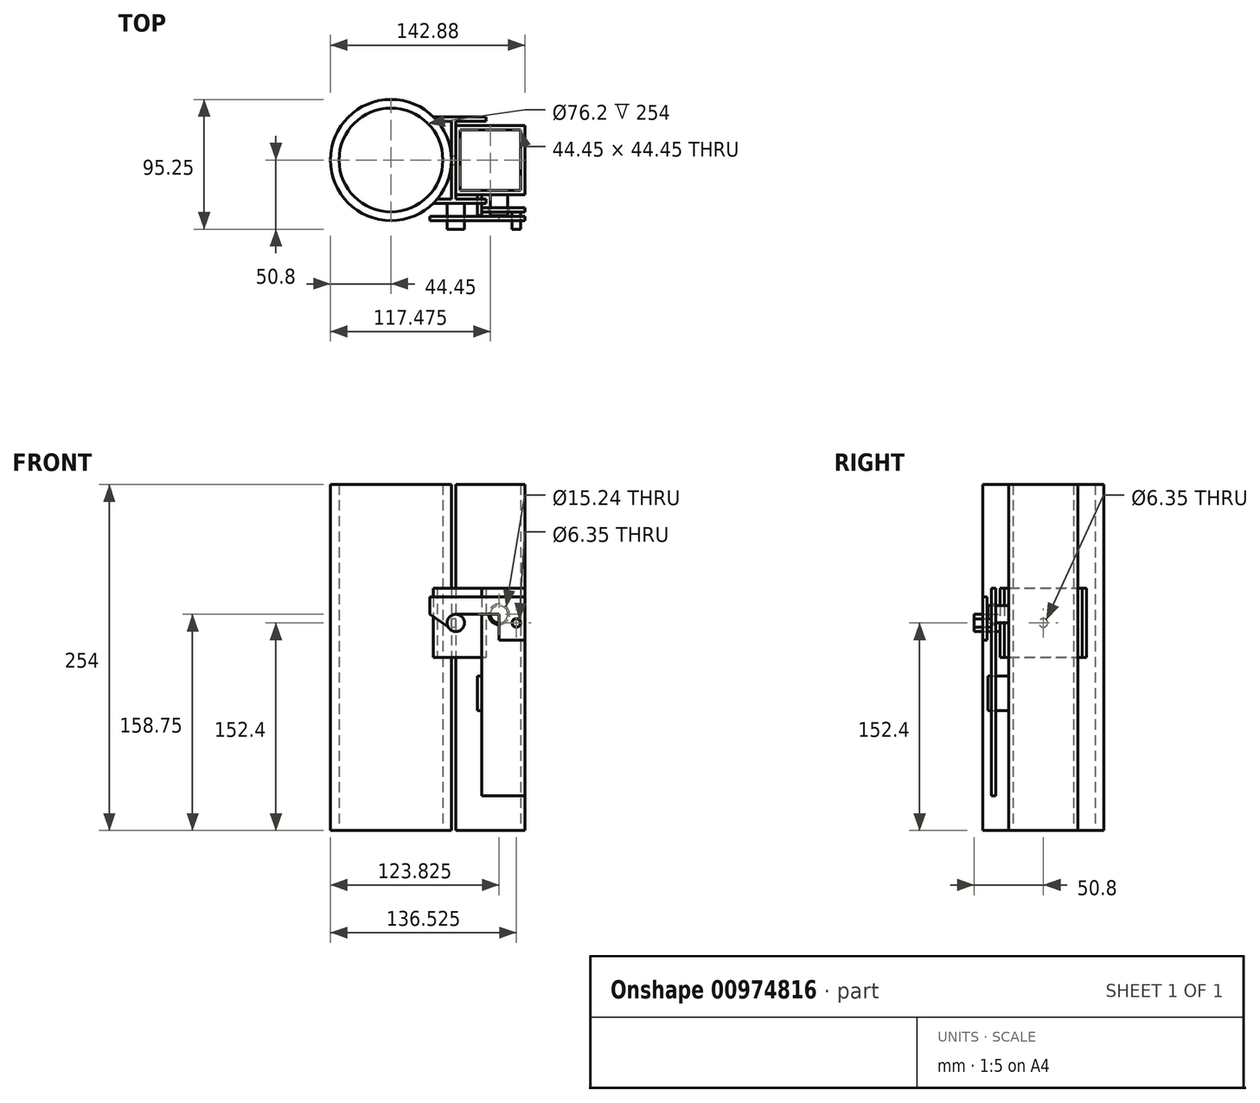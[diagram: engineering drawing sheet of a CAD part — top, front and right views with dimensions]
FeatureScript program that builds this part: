
annotation { "Feature Type Name" : "Feature", "Feature Type Description" : "" }
export const myFeature = defineFeature(function(context is Context, id is Id, definition is map)
    precondition{}
    {
        {
            var Q0;
            Q0=qCreatedBy(makeId("Top.planeOp"),FACE);
            var sketch = newSketch(context, id + "F0", { "sketchPlane" : qUnion([Q0])});
            skLineSegment(sketch, "E0", {"start": v(25.4, 31.75) * mm, "end": v(0, 31.75) * mm});
            skLineSegment(sketch, "E1", {"start": v(0, 31.75) * mm, "end": v(0, -31.75) * mm});
            skLineSegment(sketch, "E2", {"start": v(0, -31.75) * mm, "end": v(25.4, -31.75) * mm});
            skLineSegment(sketch, "E3", {"start": v(25.4, -31.75) * mm, "end": v(25.4, -28.57) * mm});
            skLineSegment(sketch, "E4", {"start": v(25.4, -28.57) * mm, "end": v(3.17, -28.57) * mm});
            skLineSegment(sketch, "E5", {"start": v(3.17, -28.57) * mm, "end": v(3.17, 28.57) * mm});
            skLineSegment(sketch, "E6", {"start": v(3.17, 28.57) * mm, "end": v(25.4, 28.57) * mm});
            skLineSegment(sketch, "E7", {"start": v(25.4, 28.57) * mm, "end": v(25.4, 31.75) * mm});
            skCircle(sketch, "E8", {"center": v(-44.45, 0) * mm, "radius": 44.45 * mm, "construction": true});
            skLineSegment(sketch, "E9", {"start": v(0, 28.57) * mm, "end": v(-10.4, 28.57) * mm});
            skLineSegment(sketch, "E10", {"start": v(0, 31.75) * mm, "end": v(-13.34, 31.75) * mm});
            skLineSegment(sketch, "E11", {"start": v(0, -28.57) * mm, "end": v(-10.4, -28.57) * mm});
            skLineSegment(sketch, "E12", {"start": v(0, -31.75) * mm, "end": v(-13.34, -31.75) * mm});
            skArc(sketch, "E13", {"start": v(-10.4, 28.57) * mm, "mid": v(-11.83, 30.2) * mm, "end": v(-13.34, 31.75) * mm});
            skArc(sketch, "E14", {"start": v(-13.34, -31.75) * mm, "mid": v(-11.83, -30.2) * mm, "end": v(-10.4, -28.57) * mm});
            skLineSegment(sketch, "E15", {"start": v(-100.23, -63.5) * mm, "end": v(128.61, -63.5) * mm, "construction": true});
            skLineSegment(sketch, "E16", {"start": v(-100.58, -69.85) * mm, "end": v(131.7, -69.85) * mm, "construction": true});
            skSolve(sketch);
        }
        {
            var Q0;
            {var subQ2=sQuery(id+"F0.wireOp",EDGE,"E9");Q0=makeQuery(id+"F0.imprint","IMPRINT",FACE,{"disambiguationData":[TD([[makeQuery(id+"F0.imprint","IMPRINT",EDGE,{"derivedFrom":subQ2}),-1.0]])]});}
            var Q1;
            {var subQ3=sQuery(id+"F0.wireOp",EDGE,"E0");Q1=makeQuery(id+"F0.imprint","IMPRINT",FACE,{"disambiguationData":[TD([[makeQuery(id+"F0.imprint","IMPRINT",EDGE,{"derivedFrom":subQ3}),1.0]])]});}
            var Q2;
            {var subQ2=sQuery(id+"F0.wireOp",EDGE,"E11");Q2=makeQuery(id+"F0.imprint","IMPRINT",FACE,{"disambiguationData":[TD([[makeQuery(id+"F0.imprint","IMPRINT",EDGE,{"derivedFrom":subQ2}),1.0]])]});}
            extrude(context, id + "F1", {"entities" : qUnion([Q0, Q1, Q2]), "depth" : 50.8 * mm, "offsetDistance" : 25.4 * mm});
        }
        {
            var Q0;
            Q0=makeQuery(id+"F1.opExtrude","SWEPT_FACE",FACE,{"disambiguationData":[OSD([sQuery(id+"F0.wireOp",EDGE,"E5")])]});
            var sketch = newSketch(context, id + "F2", { "sketchPlane" : qUnion([Q0])});
            skCircle(sketch, "E17", {"center": v(0, 25.4) * mm, "radius": 3.18 * mm});
            skSolve(sketch);
        }
        {
            var Q0;
            Q0=qSketchRegion(id+"F2",true);
            extrude(context, id + "F3", {"entities" : qUnion([Q0]), "operationType" : NewBodyOperationType.REMOVE, "endBound" : BoundingType.THROUGH_ALL, "oppositeDirection" : true, "depth" : 25.4 * mm, "offsetDistance" : 25.4 * mm});
        }
        {
            var Q0;
            Q0=qCreatedBy(makeId("Top.planeOp"),FACE);
            var sketch = newSketch(context, id + "F4", { "sketchPlane" : qUnion([Q0])});
            skCircle(sketch, "E18", {"center": v(-44.45, 0) * mm, "radius": 44.45 * mm});
            skCircle(sketch, "E19", {"center": v(-44.45, 0) * mm, "radius": 38.1 * mm});
            skLineSegment(sketch, "E20.bottom", {"start": v(3.17, 25.4) * mm, "end": v(53.97, 25.4) * mm});
            skLineSegment(sketch, "E20.top", {"start": v(3.18, -25.4) * mm, "end": v(53.98, -25.4) * mm});
            skLineSegment(sketch, "E20.left", {"start": v(3.17, 25.4) * mm, "end": v(3.18, -25.4) * mm});
            skLineSegment(sketch, "E20.right", {"start": v(53.97, 25.4) * mm, "end": v(53.98, -25.4) * mm});
            skLineSegment(sketch, "E21.bottom", {"start": v(6.35, 22.22) * mm, "end": v(50.8, 22.23) * mm});
            skLineSegment(sketch, "E21.top", {"start": v(6.35, -22.23) * mm, "end": v(50.8, -22.22) * mm});
            skLineSegment(sketch, "E21.left", {"start": v(6.35, 22.22) * mm, "end": v(6.35, -22.23) * mm});
            skLineSegment(sketch, "E21.right", {"start": v(50.8, 22.23) * mm, "end": v(50.8, -22.22) * mm});
            skSolve(sketch);
        }
        {
            var Q0;
            Q0=qSketchRegion(id+"F4",true);
            extrude(context, id + "F5", {"entities" : qUnion([Q0]), "endBound" : BoundingType.SYMMETRIC, "depth" : 254 * mm, "offsetDistance" : 25.4 * mm});
        }
        {
            var Q0;
            Q0=makeQuery(id+"F1.opExtrude","SWEPT_FACE",FACE,{"disambiguationData":[OSD([sQuery(id+"F0.wireOp",EDGE,"E2"),sQuery(id+"F0.wireOp",EDGE,"E12")])]});
            var sketch = newSketch(context, id + "F6", { "sketchPlane" : qUnion([Q0])});
            skCircle(sketch, "E22", {"center": v(3.17, 25.4) * mm, "radius": 6.35 * mm});
            skSolve(sketch);
        }
        {
            var Q0;
            Q0=qSketchRegion(id+"F6",true);
            extrude(context, id + "F7", {"entities" : qUnion([Q0]), "operationType" : NewBodyOperationType.ADD, "depth" : 19.05 * mm, "offsetDistance" : 25.4 * mm});
        }
        {
            var Q0;
            Q0=makeQuery(id+"F5.opExtrude","SWEPT_FACE",FACE,{"disambiguationData":[OSD([sQuery(id+"F4.wireOp",EDGE,"E20.top")])]});
            var sketch = newSketch(context, id + "F8", { "sketchPlane" : qUnion([Q0])});
            skCircle(sketch, "E23", {"center": v(34.93, 31.75) * mm, "radius": 6.35 * mm});
            skLineSegment(sketch, "E24.bottom", {"start": v(53.98, 50.8) * mm, "end": v(22.22, 50.8) * mm});
            skLineSegment(sketch, "E24.top", {"start": v(53.98, -101.6) * mm, "end": v(22.23, -101.6) * mm});
            skLineSegment(sketch, "E24.left", {"start": v(53.98, 50.8) * mm, "end": v(53.98, -101.6) * mm});
            skLineSegment(sketch, "E24.right", {"start": v(22.22, 50.8) * mm, "end": v(22.23, -101.6) * mm});
            skCircle(sketch, "E25", {"center": v(34.93, 31.75) * mm, "radius": 7.62 * mm});
            skLineSegment(sketch, "E26.bottom", {"start": v(22.23, -13.71) * mm, "end": v(19.05, -13.71) * mm});
            skLineSegment(sketch, "E26.top", {"start": v(22.23, -39.11) * mm, "end": v(19.05, -39.11) * mm});
            skLineSegment(sketch, "E26.left", {"start": v(22.23, -13.71) * mm, "end": v(22.23, -39.11) * mm});
            skLineSegment(sketch, "E26.right", {"start": v(19.05, -13.71) * mm, "end": v(19.05, -39.11) * mm});
            skSolve(sketch);
        }
        {
            var Q0;
            Q0=makeQuery(id+"F8.imprint","IMPRINT",FACE,{"disambiguationData":[TD([[makeQuery(id+"F8.imprint","IMPRINT",EDGE,{"derivedFrom":sQuery(id+"F8.wireOp",EDGE,"E23")}),1.0]])]});
            var Q1;
            {var subQ2=sQuery(id+"F8.wireOp",EDGE,"E26.bottom");Q1=makeQuery(id+"F8.imprint","IMPRINT",FACE,{"disambiguationData":[TD([[makeQuery(id+"F8.imprint","IMPRINT",EDGE,{"derivedFrom":subQ2}),1.0]])]});}
            extrude(context, id + "F9", {"entities" : qUnion([Q0, Q1]), "operationType" : NewBodyOperationType.ADD, "depth" : 15.24 * mm, "offsetDistance" : 25.4 * mm});
        }
        {
            var Q0;
            Q0=makeQuery(id+"F1.opExtrude","SWEPT_FACE",FACE,{"disambiguationData":[OSD([sQuery(id+"F0.wireOp",EDGE,"E2"),sQuery(id+"F0.wireOp",EDGE,"E12")])]});
            var sketch = newSketch(context, id + "F10", { "sketchPlane" : qUnion([Q0])});
            skLineSegment(sketch, "E27", {"start": v(3.17, 31.75) * mm, "end": v(53.97, 31.75) * mm});
            skLineSegment(sketch, "E28", {"start": v(53.97, 31.75) * mm, "end": v(53.97, 44.45) * mm});
            skLineSegment(sketch, "E29", {"start": v(53.97, 44.45) * mm, "end": v(-15.88, 44.45) * mm});
            skLineSegment(sketch, "E30", {"start": v(-15.88, 44.45) * mm, "end": v(-15.88, 31.75) * mm});
            skArc(sketch, "E31", {"start": v(-2.6, 22.74) * mm, "mid": v(-2.17, 28.82) * mm, "end": v(3.17, 31.75) * mm});
            skLineSegment(sketch, "E32", {"start": v(-2.6, 22.74) * mm, "end": v(-15.88, 31.75) * mm});
            skLineSegment(sketch, "E33.bottom", {"start": v(53.97, 31.75) * mm, "end": v(34.92, 31.75) * mm});
            skLineSegment(sketch, "E33.top", {"start": v(53.97, 12.7) * mm, "end": v(34.92, 12.7) * mm});
            skLineSegment(sketch, "E33.left", {"start": v(53.97, 31.75) * mm, "end": v(53.97, 12.7) * mm});
            skLineSegment(sketch, "E33.right", {"start": v(34.92, 31.75) * mm, "end": v(34.92, 12.7) * mm});
            skCircle(sketch, "E34", {"center": v(47.62, 25.4) * mm, "radius": 3.18 * mm});
            skSolve(sketch);
        }
        {
            var Q0;
            {var subQ4=sQuery(id+"F10.wireOp",EDGE,"E28");var subQ7=sQuery(id+"F10.wireOp",EDGE,"E31");var subQ18=sQuery(id+"F10.wireOp",EDGE,"E30");Q0=qUnion([makeQuery(id+"F10.imprint","IMPRINT",FACE,{"disambiguationData":[TD([[makeQuery(id+"F10.imprint","IMPRINT",EDGE,{"derivedFrom":subQ18}),1.0]])]}),makeQuery(id+"F10.imprint","IMPRINT",FACE,{"disambiguationData":[TD([[makeQuery(id+"F10.imprint","IMPRINT",EDGE,{"derivedFrom":subQ4}),1.0]])]}),makeQuery(id+"F10.imprint","IMPRINT",FACE,{"disambiguationData":[TD([[makeQuery(id+"F10.imprint","IMPRINT",EDGE,{"derivedFrom":subQ7}),-1.0]])]}),makeQuery(id+"F10.imprint","IMPRINT",FACE,{"disambiguationData":[TD([[makeQuery(id+"F10.imprint","IMPRINT",EDGE,{"derivedFrom":sQuery(id+"F10.wireOp",EDGE,"E33.top")}),-1.0]])]})]);}
            extrude(context, id + "F11", {"entities" : qUnion([Q0]), "depth" : 12.7 * mm, "offsetDistance" : 25.4 * mm, "hasSecondDirection" : true, "secondDirectionOppositeDirection" : false, "secondDirectionDepth" : 9.52 * mm});
        }
        {
            var Q0;
            {var subQ1=sQuery(id+"F8.wireOp",EDGE,"E24.bottom");Q0=makeQuery(id+"F8.imprint","IMPRINT",FACE,{"disambiguationData":[TD([[makeQuery(id+"F8.imprint","IMPRINT",EDGE,{"derivedFrom":subQ1}),1.0]])]});}
            extrude(context, id + "F12", {"entities" : qUnion([Q0]), "depth" : 12.7 * mm, "offsetDistance" : 25.4 * mm, "hasSecondDirection" : true, "secondDirectionOppositeDirection" : false, "secondDirectionDepth" : 9.52 * mm});
        }
        {
            var Q0;
            Q0=makeQuery(id+"F12.opExtrude","CAP_FACE",FACE,{"disambiguationData":[OSD([sQuery(id+"F8.wireOp",EDGE,"E24.bottom"),sQuery(id+"F8.wireOp",EDGE,"E24.top"),sQuery(id+"F8.wireOp",EDGE,"E24.left"),sQuery(id+"F8.wireOp",EDGE,"E24.right"),sQuery(id+"F8.wireOp",EDGE,"E25")])],"isStart":false});
            var sketch = newSketch(context, id + "F13", { "sketchPlane" : qUnion([Q0])});
            skCircle(sketch, "E35", {"center": v(47.63, 25.4) * mm, "radius": 3.05 * mm});
            skSolve(sketch);
        }
        {
            var Q0;
            Q0 = qSketchRegion(id + "F13", true);
            extrude(context, id + "F14", {"entities" : qUnion([Q0]), "operationType" : NewBodyOperationType.ADD, "depth" : 12.7 * mm, "offsetDistance" : 25.4 * mm});
        }
    });
